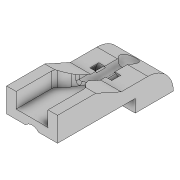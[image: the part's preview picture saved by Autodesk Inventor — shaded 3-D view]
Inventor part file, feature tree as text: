
AUTODESK INVENTOR PART (.ipt)
format: ipt  version: 2021 (Build 250183000, 183)  size: 363,520 bytes
history: native  units: mm
features: sketch x16, extrude x10, fillet x8, chamfer x6, projected_geometry x4, plane x3, revolve x2, hole x1
ambient origin geometry x8: Origin, YZ Plane, XZ Plane, XY Plane, X Axis, Y Axis, Z Axis, Center Point
bodies: Volumenkörper1 (feature_tree)
feature tree (50):
  extrude  "Extrusion1"  Depth=15.0mm
  extrude  "Extrusion2"  Depth=5.0mm
  extrude  "Extrusion3"  Depth=1.0mm
  hole  "Bohrung1"  [1 undecoded]
  fillet  "Rundung1"  Radius=10.0mm
  sketch  "Skizze5"  dims[d11=3.5mm d12=6.0mm d13=6.0mm d14=5.0mm d15=90.0deg d16=90.0mm d17=0.0mm d18=10.0mm]
  sketch  "Skizze6"  dims[d19=11.5mm]
  plane  "Arbeitsebene1"
  revolve  "Umdrehung1"
  sketch  "Skizze8"  dims[d21=5.375mm]
  plane  "Arbeitsebene2"
  revolve  "Umdrehung2"
  chamfer  "Fase1"  Distance=1.0mm Angle=45.0deg
  chamfer  "Fase2"  Distance=1.0mm Angle=45.0deg
  extrude  "Extrusion4"  Depth=12.5mm
  extrude  "Extrusion5"  Depth=20.0mm
  extrude  "Extrusion6"  Depth=0.5mm TaperAngle=0.0deg
  extrude  "Extrusion7"  Depth=5.0mm
  fillet  "Rundung2"  Radius=5.0mm
  fillet  "Rundung3"  Radius=5.0mm
  chamfer  "Fase4"  Distance=2.0mm
  chamfer  "Fase5"  Distance=4.0mm
  chamfer  "Fase6"  Distance=4.5mm
  extrude  "Extrusion8"  Depth=5.0mm TaperAngle=0.0deg
  chamfer  "Fase7"  Distance=10.0mm
  fillet  "Rundung9"  Radius=2.0mm
  fillet  "Rundung10"  Radius=10.0mm
  plane  "Arbeitsebene3"
  extrude  "Extrusion10"  Depth=10.0mm TaperAngle=45.0deg
  extrude  "Extrusion11"  Depth=1.0mm TaperAngle=45.0deg
  fillet  "Rundung12"  Radius=18.0mm
  fillet  "Rundung13"  Radius=1.0mm
  fillet  "Rundung14"  Radius=2.0mm
  sketch  "Skizze1"  dims[d0=20.0mm d1=15.0mm]
  sketch  "Skizze2"  dims[d2=5.0mm d3=0.0mm d4=5.8mm]
  sketch  "Skizze3"  dims[d5=1.0mm d6=0.0mm d7=20.0mm]
  sketch  "Skizze4"  dims[d8=30.5mm d9=5.0mm d10=0.0mm]
  projected_geometry  "Projizierte Kontur1"
  sketch  "Skizze7"  dims[d20=5.375mm]
  sketch  "Skizze9"  dims[d22=3.0mm]
  sketch  "Skizze10"  dims[d23=9.75mm]
  sketch  "Skizze11"  dims[d24=90.0deg]
  projected_geometry  "Projizierte Kontur2"
  sketch  "Skizze12"  dims[d25=25.75mm]
  sketch  "Skizze13"  dims[d26=90.0deg d27=1.0mm d28=2.0mm d29=45.0deg d30=1.0mm d31=2.0mm d32=45.0deg]
  sketch  "Skizze15"  dims[d33=12.5mm d34=30.0mm]
  projected_geometry  "Projizierte Kontur3"
  projected_geometry  "Projizierte Kontur4"
  sketch  "Skizze17"  dims[d35=1.5mm d36=0.0mm d37=20.0mm]
  sketch  "Skizze18"  dims[d38=25.0mm d39=4.5mm d40=0.0mm d41=5.0mm d42=5.0mm d43=5.0mm d44=2.0mm d45=4.0mm d46=4.5mm d47=0.0mm d48=5.0mm d49=0.0mm d53=10.0mm d54=2.0mm d57=10.0mm d58=4.5mm d59=45.0deg d60=10.0mm d61=4.5mm d62=45.0deg d68=1.0mm d69=2.0mm d70=45.0deg d71=18.0mm d72=0.0mm d73=1.0mm d74=2.0mm d75=45.0deg d76=2.0mm d77=2.0mm d85=11.26mm d86=3.5mm d87=0.0mm d88=9.0mm d89=2.4mm d90=10.0mm d91=0.0mm d92=1.0mm d93=1.0mm d94=0.5mm]
note: 1 required parameter value undecoded (feature->parameter linkage not recoverable at this tier; creation-order binding heuristic only, values carry confidence <= 0.55)
